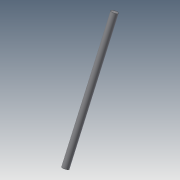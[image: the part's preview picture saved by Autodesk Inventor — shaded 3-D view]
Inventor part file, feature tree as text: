
AUTODESK INVENTOR PART (.ipt)
format: ipt  version: 2014 SP1 (Build 180222100, 222)  size: 103,936 bytes
history: native  units: in
note: dims shown in document units (in); Inventor stores cm internally (conversion verified against a paired STEP export)
features: extrude x3, sketch x3, reference x2
ambient origin geometry x8: Origin, YZ Plane, XZ Plane, XY Plane, X Axis, Y Axis, Z Axis, Center Point
bodies: Solid1 (feature_tree)
feature tree (8):
  extrude  "Extrusion1"  Depth=0.1649in
  extrude  "Extrusion2"  Depth=0.7874in TaperAngle=0.0deg
  extrude  "Extrusion3"  [1 undecoded]
  sketch  "Sketch1"  dims[d1=0.1649in d3=0.1649in]
  reference  "Reference1"
  reference  "Reference2"
  sketch  "Sketch2"  dims[d4=0.036in d5=0.0in d6=0.7874in d7=0.0in]
  sketch  "Sketch3"  dims[d8=0.3445in d9=0.0in]
note: 1 required parameter value undecoded (feature->parameter linkage not recoverable at this tier; creation-order binding heuristic only, values carry confidence <= 0.55)
